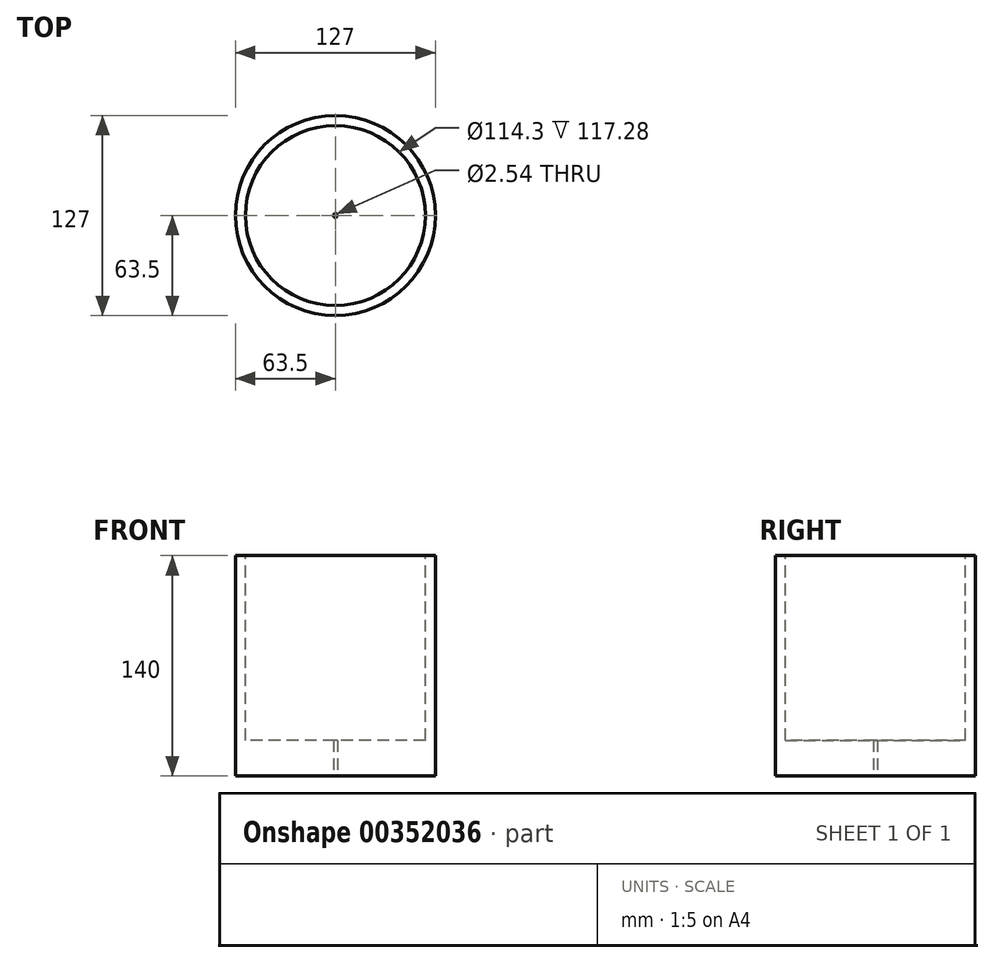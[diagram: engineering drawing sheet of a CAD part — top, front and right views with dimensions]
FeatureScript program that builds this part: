
annotation { "Feature Type Name" : "Feature", "Feature Type Description" : "" }
export const myFeature = defineFeature(function(context is Context, id is Id, definition is map)
    precondition{}
    {
        {
            var Q0;
            Q0=qCreatedBy(makeId("Top.planeOp"),FACE);
            var sketch = newSketch(context, id + "F0", { "sketchPlane" : qUnion([Q0])});
            skCircle(sketch, "E0", {"center": v(0, 0) * mm, "radius": 63.5 * mm});
            skCircle(sketch, "E1", {"center": v(0, 0) * mm, "radius": 57.15 * mm});
            skSolve(sketch);
        }
        {
            var Q0;
            Q0=makeQuery(id+"F0.imprint","IMPRINT",FACE,{"disambiguationData":[TD([[makeQuery(id+"F0.imprint","IMPRINT",EDGE,{"derivedFrom":sQuery(id+"F0.wireOp",EDGE,"E1")}),1.0]])]});
            var Q1;
            Q1=makeQuery(id+"F0.imprint","IMPRINT",FACE,{"disambiguationData":[TD([[makeQuery(id+"F0.imprint","IMPRINT",EDGE,{"derivedFrom":sQuery(id+"F0.wireOp",EDGE,"E0")}),1.0]])]});
            extrude(context, id + "F1", {"entities" : qUnion([Q0, Q1]), "depth" : 140 * mm});
        }
        {
            var Q0;
            Q0=qCreatedBy(makeId("Top.planeOp"),FACE);
            var sketch = newSketch(context, id + "F2", { "sketchPlane" : qUnion([Q0])});
            skCircle(sketch, "E2", {"center": v(0, 0) * mm, "radius": 57.15 * mm});
            skSolve(sketch);
        }
        {
            var Q0;
            Q0=makeQuery(id+"F2.imprint","IMPRINT",FACE,{"disambiguationData":[TD([[makeQuery(id+"F2.imprint","IMPRINT",EDGE,{"derivedFrom":sQuery(id+"F2.wireOp",EDGE,"E2")}),1.0]])]});
            extrude(context, id + "F3", {"entities" : qUnion([Q0]), "operationType" : NewBodyOperationType.ADD, "depth" : 172.72 * mm});
        }
        {
            var Q0;
            Q0=makeQuery(id+"F3.opExtrude","CAP_FACE",FACE,{"disambiguationData":[OSD([sQuery(id+"F2.wireOp",EDGE,"E2")])],"isStart":false});
            var Q1;
            Q1=makeQuery(id+"F1.opExtrude","CAP_FACE",FACE,{"disambiguationData":[OSD([sQuery(id+"F0.wireOp",EDGE,"E0")])],"isStart":true});
            extrude(context, id + "F4", {"entities" : qUnion([Q0, Q1]), "operationType" : NewBodyOperationType.REMOVE, "oppositeDirection" : true, "depth" : 150 * mm});
        }
        {
            var Q0;
            Q0=qCreatedBy(makeId("Top.planeOp"),FACE);
            var sketch = newSketch(context, id + "F5", { "sketchPlane" : qUnion([Q0])});
            skCircle(sketch, "E3", {"center": v(0, 0) * mm, "radius": 1.27 * mm});
            skSolve(sketch);
        }
        {
            var Q0;
            Q0=makeQuery(id+"F5.imprint","IMPRINT",FACE,{"disambiguationData":[TD([[makeQuery(id+"F5.imprint","IMPRINT",EDGE,{"derivedFrom":sQuery(id+"F5.wireOp",EDGE,"E3")}),1.0]])]});
            extrude(context, id + "F6", {"entities" : qUnion([Q0]), "operationType" : NewBodyOperationType.REMOVE, "endBound" : BoundingType.THROUGH_ALL, "depth" : 25.4 * mm});
        }
    });
